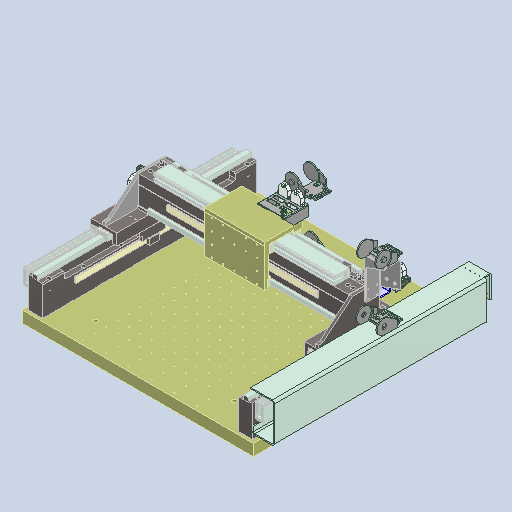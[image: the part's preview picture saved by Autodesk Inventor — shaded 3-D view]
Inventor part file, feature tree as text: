
AUTODESK INVENTOR PART (.ipt)
format: ipt  version: 2022 (Build 260153000, 153)  size: 2,744,832 bytes
history: native  units: in
note: dims shown in document units (in); Inventor stores cm internally (conversion verified against a paired STEP export)
features: other x34, mirror x3, sheet_metal_op x2, extrude x1
ambient origin geometry x8: Origin, YZ Plane, XZ Plane, XY Plane, X Axis, Y Axis, Z Axis, Center Point
bodies: Solid1 (feature_tree), Solid2 (feature_tree), Solid3 (feature_tree), Solid4 (feature_tree), Solid5 (feature_tree), Solid6 (feature_tree), Solid7 (feature_tree), Solid8 (feature_tree), Solid9 (feature_tree), Solid10 (feature_tree), Solid11 (feature_tree), Solid12 (feature_tree), Solid13 (feature_tree), Solid14 (feature_tree), Solid15 (feature_tree), Solid16 (feature_tree), Solid17 (feature_tree), Solid18 (feature_tree), Solid19 (feature_tree), Solid20 (feature_tree), Solid21 (feature_tree), Solid22 (feature_tree), Solid23 (feature_tree), Solid24 (feature_tree), Solid25 (feature_tree), Solid26 (feature_tree), Solid27 (feature_tree), Solid28 (feature_tree), Solid29 (feature_tree), Solid30 (feature_tree), Solid31 (feature_tree), Solid32 (feature_tree), Solid33 (feature_tree), Solid34 (feature_tree), Solid35 (feature_tree), Solid36 (feature_tree), Solid37 (feature_tree), Solid38 (feature_tree), Solid39 (feature_tree), Solid40 (feature_tree)
feature tree (40):
  mirror  "MIRROR4"
  other  "MCM01114-1-SOLID1"
  other  "MCA01286-1-SOLID1"
  other  "MCM01114-1-SOLID2"
  other  "25PINCONN WITH SHELL-2-SOLID1"
  other  "25PINCONN WITH SHELL-2-SOLID1:1"
  other  "BASE CHAMFER"
  other  "M4X0.7 TAPPED P-CLAMP 2"
  other  "25PINCONN WITH SHELL-3-SOLID1"
  sheet_metal_op  "FACE2092"
  other  "MCM01114-1-SOLID1:1"
  sheet_metal_op  "FACE2229"
  other  "25PINCONN WITH SHELL-4-SOLID1"
  other  "MCM01114-1-SOLID2:1"
  other  "25PINCONN WITH SHELL-4-SOLID1:1"
  other  "MCM01114-1-SOLID3"
  other  "FACE2229:1"
  other  "25PINCONN WITH SHELL-5-SOLID1"
  other  "MCM01114-1-SOLID2:2"
  mirror  "MIRROR4:1"
  other  "MCA03023-1-SOLID2"
  other  "M20X2.5 TAPPED HOLE1"
  mirror  "MIRROR4:2"
  other  "FACE2092:1"
  other  "25PINCONN WITH SHELL-3-SOLID1:1"
  other  "MCM01114-1-SOLID3:1"
  other  "MCM01114-1-SOLID3:2"
  other  "MCM01114-1-SOLID1:2"
  other  "25PINCONN WITH SHELL-2-SOLID1:2"
  other  "25PINCONN WITH SHELL-6-SOLID1"
  other  "MCA01286-1-SOLID1:1"
  other  "M6X1.0 TAPPED HOLE1"
  other  "BASE CHAMFER:1"
  other  "25PINCONN WITH SHELL-1-SOLID1"
  other  "M4X0.7 TAPPED PEM NUT"
  other  "MCA03023-1-SOLID1"
  other  "25PINCONN WITH SHELL-1-SOLID1:1"
  other  "LPATTERN3"
  extrude  "EXTRUDE6"  [1 undecoded]
  other  "25PINCONN WITH SHELL-1-SOLID1:2"
note: 1 required parameter value undecoded (feature->parameter linkage not recoverable at this tier; creation-order binding heuristic only, values carry confidence <= 0.55)
